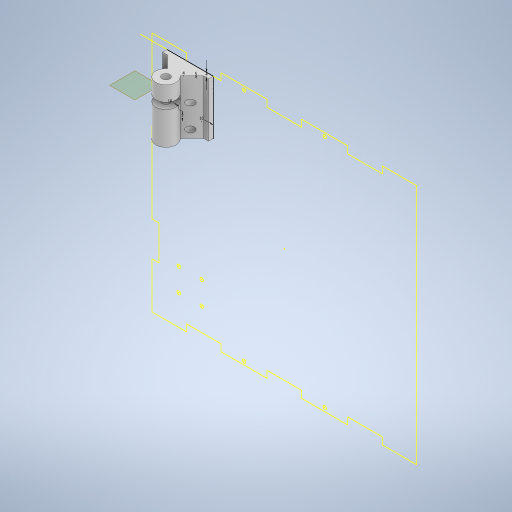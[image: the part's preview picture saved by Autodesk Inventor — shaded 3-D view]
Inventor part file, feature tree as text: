
AUTODESK INVENTOR PART (.ipt)
format: ipt  version: 2024.2 (Build 282272000, 272)  size: 330,240 bytes
history: native  units: mm
features: other x6, extrude x5, sketch x4, reference x3, chamfer x2
ambient origin geometry x8: Origin, YZ Plane, XZ Plane, XY Plane, X Axis, Y Axis, Z Axis, Center Point
bodies: Body1 (feature_tree)
feature tree (20):
  other  "Твердое тело1"
  sketch  "Эскиз1"
  extrude  "Выдавливание1"  Depth=10.0mm
  other  "РабПлоскость1"
  extrude  "Выдавливание3"  Depth=10.0mm
  extrude  "Выдавливание4"  Depth=7.0mm
  chamfer  "Фаска3"  Distance=4.0mm
  chamfer  "Фаска4"  Distance=5.0mm
  extrude  "Выдавливание5"  Depth=4.0mm
  extrude  "Выдавливание6"  Depth=4.0mm TaperAngle=0.0deg
  reference  "Ссылка1"
  reference  "Ссылка2"
  reference  "Ссылка3"
  sketch  "Эскиз2"
  sketch  "Эскиз3"
  sketch  "Эскиз4"
  other  "<userpath>\Documents\Artist-v2\3D\Робот.iam"
  other  "Робот.iam"
  other  "бок:1"
  other  "Низ робота:1"
